# Revit family: HVAC_Electric-Humidifier_Neptronic_SKE4-SDU
name_source: partatom
category: Mechanical Equipment
units: mm (PartAtom-declared; Revit-internal decimal feet)

## family parameters
Classification = None
Cut with Voids When Loaded = No
Host = Face
Part Type = Normal
Room Calculation Point = No
Round Connector Dimension = Use Diameter
Shared = No

## types (16) — shared parameters
Apparent Load = 0 VA
Default Elevation = 48.00 in
Depth = 0.00 in
Description = SDU for SKE4-E Steam Humidifier
Manufacturer = Neptronic
Material = Neptronic - Stainless Steel - Painted Blue
Number of Poles = 1
Operating Weight = 0.00 kgf
Operating Weight - Mass = 0.00 lb
Product Material = Neptronic - Stainless Steel - Painted Blue
Product Page URL = https://www.neptronic.com
Rated Load Current = 0.00 A
Rated Power = 0 W
Shipping Weight = 0.00 kgf
Shipping Weight - Mass = 0.00 lb
URL = https://www.neptronic.com
Version = 1
Weight - Mass = 0.00 lb
Width = 13.86 in
zero-valued in all types: Power Factor

## per-type parameters (varying)
| type | Dimension A | Dimension B | Dimension C | Dimension D | Dimension E | Frequency | Height | Length | Main Drain Outlet Diameter | Model | Rated Capacity | Rated Current | Region | Steam Inlet Diameter | Voltage | Weight | z_SDU Unit Height |
| SDU4-2-480-1 | 19.25 in | 7.50 in | 14.90 in | 1.00 in | 1.75 in | 60 Hz | 14.90 in | 22.25 in | 0.00 in | SDU4-2 | 40 lb/h | 0.20 A | N | 1.38 in | 480 V | 9.07 kgf | 7.40 in |
| SDU4-3-600-1 | 19.25 in | 7.50 in | 18.90 in | 1.00 in | 1.75 in | 60 Hz | 18.90 in | 22.25 in | 0.50 in | SDU4-3 | 96 lb/h | 0.20 A | N | 2.00 in | 600 V | 13.61 kgf | 11.40 in |
| SDU4-3-480-1 | 19.25 in | 7.50 in | 18.90 in | 1.00 in | 1.75 in | 60 Hz | 18.90 in | 22.25 in | 0.50 in | SDU4-3 | 96 lb/h | 0.20 A | N | 2.00 in | 480 V | 13.61 kgf | 11.40 in |
| SDU4-2-600-1 | 19.25 in | 7.50 in | 14.90 in | 1.00 in | 1.75 in | 60 Hz | 14.90 in | 22.25 in | 0.00 in | SDU4-2 | 40 lb/h | 0.20 A | N | 1.38 in | 600 V | 9.07 kgf | 7.40 in |
| SDU4-1-208-1 | 16.38 in | 6.75 in | 13.70 in | 0.75 in | 1.13 in | 60 Hz | 13.70 in | 19.38 in | 0.00 in | SDU4-1 | 18 lb/h | 0.20 A | N | 1.38 in | 208 V | 6.80 kgf | 6.95 in |
| SDU4-1-240-1 | 16.38 in | 6.75 in | 13.70 in | 0.75 in | 1.13 in | 60 Hz | 13.70 in | 19.38 in | 0.00 in | SDU4-1 | 18 lb/h | 0.20 A | N | 1.38 in | 240 V | 6.80 kgf | 6.95 in |
| SDU4-1-480-1 | 16.38 in | 6.75 in | 13.70 in | 0.75 in | 1.13 in | 60 Hz | 13.70 in | 19.38 in | 0.00 in | SDU4-1 | 18 lb/h | 0.10 A | N | 1.38 in | 480 V | 6.80 kgf | 6.95 in |
| SDU4-1-600-1 | 16.38 in | 6.75 in | 13.70 in | 0.75 in | 1.13 in | 60 Hz | 13.70 in | 19.38 in | 0.00 in | SDU4-1 | 18 lb/h | 0.10 A | N | 1.38 in | 600 V | 6.80 kgf | 6.95 in |
| SDU4-3-208-1 | 18.50 in | 7.50 in | 18.90 in | 1.00 in | 1.75 in | 60 Hz | 18.90 in | 21.50 in | 0.50 in | SDU4-3 | 96 lb/h | 0.40 A | N | 2.00 in | 208 V | 13.61 kgf | 11.40 in |
| SDU4-2-208-1 | 19.25 in | 7.50 in | 14.90 in | 1.00 in | 1.75 in | 60 Hz | 14.90 in | 22.25 in | 0.00 in | SDU4-2 | 40 lb/h | 0.40 A | N | 1.38 in | 208 V | 9.07 kgf | 7.40 in |
| SDU4-1-120-1 | 16.38 in | 6.75 in | 13.70 in | 0.75 in | 1.13 in | 60 Hz | 13.70 in | 19.38 in | 0.00 in | SDU4-1 | 18 lb/h | 0.30 A | N | 1.38 in | 120 V | 6.80 kgf | 6.95 in |
| SDU4-1-230-1 | 15.98 in | 6.73 in | 13.70 in | 0.75 in | 1.14 in | 50 Hz | 13.70 in | 18.98 in | 0.00 in | SDU4-1 | 18 lb/h | 0.20 A | E | 1.38 in | 230 V | 7.00 kgf | 6.97 in |
| SDU4-1-400-1 | 15.98 in | 6.73 in | 13.70 in | 0.75 in | 0.75 in | 50 Hz | 13.70 in | 18.98 in | 0.00 in | SDU4-1 | 18 lb/h | 0.20 A | E | 1.38 in | 400 V | 7.00 kgf | 6.97 in |
| SDU4-2-230-1 | 18.50 in | 7.52 in | 14.84 in | 0.98 in | 1.77 in | 50 Hz | 14.84 in | 21.50 in | 0.00 in | SDU4-2 | 40 lb/h | 0.30 A | E | 1.38 in | 230 V | 9.00 kgf | 7.32 in |
| SDU4-2-400-1 | 18.50 in | 7.52 in | 14.84 in | 0.98 in | 1.77 in | 50 Hz | 14.84 in | 21.50 in | 0.00 in | SDU4-2 | 40 lb/h | 0.20 A | E | 1.38 in | 400 V | 9.00 kgf | 7.32 in |
| SDU4-3-400-1 | 18.50 in | 7.52 in | 18.90 in | 0.98 in | 1.77 in | 50 Hz | 18.90 in | 21.50 in | 0.00 in | SDU4-3 | 96 lb/h | 0.20 A | E | 1.38 in | 230 V | 14.00 kgf | 11.38 in |

## geometry (parser evidence)
native form markers: Sweep x21
no freeform markers — native parametric forms only
